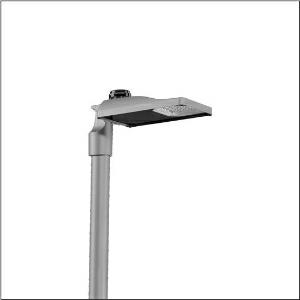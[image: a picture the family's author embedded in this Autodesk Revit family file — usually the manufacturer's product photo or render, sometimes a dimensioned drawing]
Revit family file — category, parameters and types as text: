
# Revit family: streetlight_sl_31_micro___st1_5a_5xh1p7bn08ca_d18d
name_source: partatom
category: Lighting Fixtures
units: mm (PartAtom-declared; Revit-internal decimal feet)

## family parameters
Cut with Voids When Loaded = No
Host = Face
Light Source = No
Part Type = Normal
Room Calculation Point = No
Round Connector Dimension = Use Diameter
Shared = No

## types (1)
- --- (1 x LED, 1150 lm, 10.3 W, 2200K)
    Apparent Load = 10 VA
    CIE Flux Codes = 22 53 95 100 100
    Color Rendering = 70
    Color Temperature = 2200K
    Default Elevation = 1800 mm
    Description = Streetlight SL 31 micro NEMA (7pin) mast luminaire for post-top, side-entry; light control with lens of PMMA; light distribution: ST1.5a, direct asymmetric distribution, for standard-compliant lighting for roads and squares; LED: luminous flux: 1.150lm, light colour: 722, colour temperature: 2200K; luminous efficacy: 111,7lm/W; control: overheat protection, intelligent temperature release in ECG and LED module, constant luminous flux control, time-dependent luminous flux control, flexible luminous flux parameterisation, pre-setting: linear dimming characteristic; luminaire housing, of diecast aluminium, Siteco® metallic grey (DB 702S), corrosivity category C5 high according to DIN EN ISO 12944; cover of toughened safety glass, transparent, mast flange of diecast aluminium, Siteco® metallic grey (DB 702S), spigot size: 76/60mm, mast flange included unmounted; with cable H07RN-F 3x 1.5mm², cable length: 5,5m, connection cable pre-assembled; mains connection: 220..240V, AC, 50/60Hz; power consumption (at start of service life): 10,3W / (at end of service life): 10,6W / (with reduced operation 50%): 5,3W; protection rating (complete): IP66; insulation class (complete): insulation class I (protective earthing); impact resistance: IK10; certification: CE, ENEC, ENEC+, VDE, UKCA; permissible operating ambient temperature for outdoor applications: -40..+50°C; packaging unit: 1 piece

Light Distribution: ST1.5a
    Height = 76 mm
    Lamp = 1 x LED
    Lamp Light Flux = 1150 lm
    Lamp Power = 10.3 W
    Lamp count = 1
    Length = 467 mm
    Luminous efficacy = 112 lm/W
    Manufacturer = Siteco
    ModVariant = No
    Model = 5XH1P7BN08CA
    Number of Poles = 1
    OnlyDefault = Yes
    Power Factor = 1
    Product Name = Streetlight SL 31 micro | ST1.5a
    Product group = mast luminaire | pylon top
    ProductGroupID = 6100
    Protection Class = Protection class I
    Protection Degree = IP 66
    RLX_Detail_Level = 1
    RLX_Emergency_Light_Flux = 0 lm
    RLX_Emergency_Type = 0
    RLX_Emergency_Type_DB = No
    RlxData = <blob elided: 26393 chars, md5=025bb05b>
    Socket = socket
    Standby Power = 0 W
    System Light Flux = 1150 lm
    System Power = 10 W
    Type Comments = factory setting: luminous flux: 100 % | dim-lin: 254 | 386 mA
    Type Image = l_1300305.jpg
    URL = http://relux.com
    VarID = @adj_009195
    Voltage = 0 V
    Weight = 0.00 kg
    Width = 265 mm

## geometry (parser evidence)
native form markers: Blend x4, Sweep x11
no freeform markers — native parametric forms only
